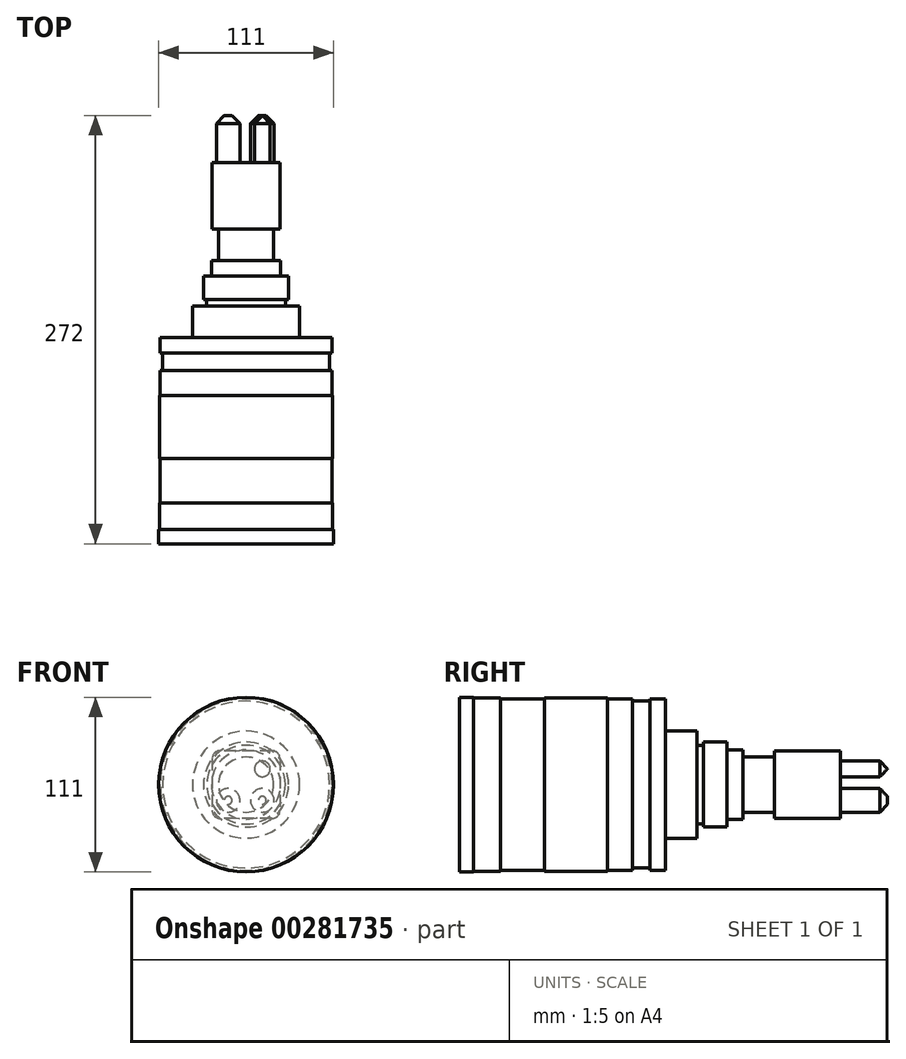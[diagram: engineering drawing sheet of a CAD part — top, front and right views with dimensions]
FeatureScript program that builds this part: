
annotation { "Feature Type Name" : "Feature", "Feature Type Description" : "" }
export const myFeature = defineFeature(function(context is Context, id is Id, definition is map)
    precondition{}
    {
        {
            var Q0;
            Q0=qCreatedBy(makeId("Right.planeOp"),FACE);
            var sketch = newSketch(context, id + "F0", { "sketchPlane" : qUnion([Q0])});
            skLineSegment(sketch, "E0", {"start": v(-113.88, 0) * mm, "end": v(-113.88, 55.5) * mm});
            skLineSegment(sketch, "E1", {"start": v(-113.88, 55.5) * mm, "end": v(-104.88, 55.5) * mm});
            skLineSegment(sketch, "E2", {"start": v(-104.88, 55.5) * mm, "end": v(-104.88, 55) * mm});
            skLineSegment(sketch, "E3", {"start": v(-104.88, 55) * mm, "end": v(-87.88, 55) * mm});
            skLineSegment(sketch, "E4", {"start": v(-87.88, 55) * mm, "end": v(-87.88, 54.5) * mm});
            skLineSegment(sketch, "E5", {"start": v(-87.88, 54.5) * mm, "end": v(-59.88, 54.5) * mm});
            skLineSegment(sketch, "E6", {"start": v(-59.88, 54.5) * mm, "end": v(-59.88, 55) * mm});
            skLineSegment(sketch, "E7", {"start": v(-59.88, 55) * mm, "end": v(-19.88, 55) * mm});
            skLineSegment(sketch, "E8", {"start": v(-19.88, 55) * mm, "end": v(-19.88, 54.5) * mm});
            skLineSegment(sketch, "E9", {"start": v(-19.88, 54.5) * mm, "end": v(-3.88, 54.5) * mm});
            skLineSegment(sketch, "E10", {"start": v(-3.88, 54.5) * mm, "end": v(-3.88, 53) * mm});
            skLineSegment(sketch, "E11", {"start": v(-3.88, 53) * mm, "end": v(7.12, 53) * mm});
            skLineSegment(sketch, "E12", {"start": v(7.12, 53) * mm, "end": v(7.12, 54.5) * mm});
            skLineSegment(sketch, "E13", {"start": v(7.12, 54.5) * mm, "end": v(17.12, 54.5) * mm});
            skLineSegment(sketch, "E14", {"start": v(17.12, 54.5) * mm, "end": v(17.12, 34) * mm});
            skLineSegment(sketch, "E15", {"start": v(17.12, 34) * mm, "end": v(37.12, 34) * mm});
            skLineSegment(sketch, "E16", {"start": v(37.12, 34) * mm, "end": v(37.12, 25) * mm});
            skLineSegment(sketch, "E17", {"start": v(37.12, 25) * mm, "end": v(41.12, 25) * mm});
            skLineSegment(sketch, "E18", {"start": v(41.12, 25) * mm, "end": v(41.12, 27) * mm});
            skLineSegment(sketch, "E19", {"start": v(41.12, 27) * mm, "end": v(56.12, 27) * mm});
            skLineSegment(sketch, "E20", {"start": v(56.12, 27) * mm, "end": v(56.12, 22) * mm});
            skLineSegment(sketch, "E21", {"start": v(56.12, 22) * mm, "end": v(66.12, 22) * mm});
            skLineSegment(sketch, "E22", {"start": v(66.12, 22) * mm, "end": v(66.12, 17.5) * mm});
            skLineSegment(sketch, "E23", {"start": v(66.12, 17.5) * mm, "end": v(86.12, 17.5) * mm});
            skLineSegment(sketch, "E24", {"start": v(86.12, 17.5) * mm, "end": v(86.12, 0) * mm});
            skLineSegment(sketch, "E25", {"start": v(-113.88, 0) * mm, "end": v(86.12, 0) * mm});
            skLineSegment(sketch, "E26", {"start": v(-143.44, 0) * mm, "end": v(122.9, 0) * mm, "construction": true});
            skSolve(sketch);
        }
        {
            var Q0;
            Q0=makeQuery(id+"F0.imprint","IMPRINT",FACE,{"disambiguationData":[TD([[makeQuery(id+"F0.imprint","IMPRINT",EDGE,{"derivedFrom":sQuery(id+"F0.wireOp",EDGE,"E0")}),-1.0]])]});
            var Q1;
            Q1=sQuery(id+"F0.wireOp",EDGE,"E26");
            revolve(context, id + "F1", {"entities" : qUnion([Q0]), "axis" : qUnion([Q1]), "revolveType" : RevolveType.FULL});
        }
        {
            var Q0;
            Q0=makeQuery(id+"F1.opRevolve","SWEPT_FACE",FACE,{"disambiguationData":[OSD([sQuery(id+"F0.wireOp",EDGE,"E24")])]});
            var sketch = newSketch(context, id + "F2", { "sketchPlane" : qUnion([Q0])});
            skLineSegment(sketch, "E27.bottom", {"start": v(-16.5, 21.5) * mm, "end": v(16.5, 21.5) * mm});
            skLineSegment(sketch, "E27.top", {"start": v(-16.5, -21.5) * mm, "end": v(16.5, -21.5) * mm});
            skLineSegment(sketch, "E27.left", {"start": v(-21.5, 16.5) * mm, "end": v(-21.5, -16.5) * mm});
            skLineSegment(sketch, "E27.right", {"start": v(21.5, 16.5) * mm, "end": v(21.5, -16.5) * mm});
            skPoint(sketch, "E27.middle", {"position": v(0, 0) * mm});
            skPoint(sketch, "E28.visualSharp", {"position": v(-21.5, 21.5) * mm});
            skArc(sketch, "E28.filletArc", {"start": v(-16.5, 21.5) * mm, "mid": v(-20.04, 20.04) * mm, "end": v(-21.5, 16.5) * mm});
            skPoint(sketch, "E29.visualSharp", {"position": v(21.5, 21.5) * mm});
            skArc(sketch, "E29.filletArc", {"start": v(21.5, 16.5) * mm, "mid": v(20.04, 20.04) * mm, "end": v(16.5, 21.5) * mm});
            skPoint(sketch, "E30.visualSharp", {"position": v(21.5, -21.5) * mm});
            skArc(sketch, "E30.filletArc", {"start": v(16.5, -21.5) * mm, "mid": v(20.04, -20.04) * mm, "end": v(21.5, -16.5) * mm});
            skPoint(sketch, "E31.visualSharp", {"position": v(-21.5, -21.5) * mm});
            skArc(sketch, "E31.filletArc", {"start": v(-21.5, -16.5) * mm, "mid": v(-20.04, -20.04) * mm, "end": v(-16.5, -21.5) * mm});
            skSolve(sketch);
        }
        {
            var Q0;
            Q0=makeQuery(id+"F2.imprint","IMPRINT",FACE,{"disambiguationData":[TD([[makeQuery(id+"F2.imprint","IMPRINT",EDGE,{"derivedFrom":makeQuery(id+"F1.opRevolve","SWEPT_EDGE",EDGE,{"disambiguationData":[OSD([sQuery(id+"F0.wireOp",EDGE,"E23"),sQuery(id+"F0.wireOp",EDGE,"E24")])]})}),-1.0]])]});
            var Q1;
            Q1=makeQuery(id+"F2.imprint","IMPRINT",FACE,{"disambiguationData":[TD([[makeQuery(id+"F2.imprint","IMPRINT",EDGE,{"derivedFrom":sQuery(id+"F2.wireOp",EDGE,"E27.bottom")}),-1.0]])]});
            extrude(context, id + "F3", {"entities" : qUnion([Q0, Q1]), "depth" : 42 * mm});
        }
        {
            var Q0;
            Q0=makeQuery(id+"F3.opExtrude","CAP_FACE",FACE,{"disambiguationData":[OSD([sQuery(id+"F2.wireOp",EDGE,"E27.bottom"),sQuery(id+"F2.wireOp",EDGE,"E27.top"),sQuery(id+"F2.wireOp",EDGE,"E27.left"),sQuery(id+"F2.wireOp",EDGE,"E27.right"),sQuery(id+"F2.wireOp",EDGE,"E28.filletArc"),sQuery(id+"F2.wireOp",EDGE,"E29.filletArc"),sQuery(id+"F2.wireOp",EDGE,"E30.filletArc"),sQuery(id+"F2.wireOp",EDGE,"E31.filletArc")])],"isStart":false});
            var sketch = newSketch(context, id + "F4", { "sketchPlane" : qUnion([Q0])});
            skCircle(sketch, "E32", {"center": v(-10.33, 9.97) * mm, "radius": 5 * mm});
            skCircle(sketch, "E33", {"center": v(-10.33, -10.03) * mm, "radius": 7.5 * mm});
            skCircle(sketch, "E34", {"center": v(11.38, -10.03) * mm, "radius": 7.5 * mm});
            skLineSegment(sketch, "E35", {"start": v(-10.33, -10.03) * mm, "end": v(11.38, -10.03) * mm, "construction": true});
            skLineSegment(sketch, "E36", {"start": v(-10.33, 9.97) * mm, "end": v(-10.33, -10.03) * mm, "construction": true});
            skSolve(sketch);
        }
        {
            var Q0;
            Q0=makeQuery(id+"F4.imprint","IMPRINT",FACE,{"disambiguationData":[TD([[makeQuery(id+"F4.imprint","IMPRINT",EDGE,{"derivedFrom":sQuery(id+"F4.wireOp",EDGE,"E32")}),1.0]])]});
            var Q1;
            Q1=makeQuery(id+"F4.imprint","IMPRINT",FACE,{"disambiguationData":[TD([[makeQuery(id+"F4.imprint","IMPRINT",EDGE,{"derivedFrom":sQuery(id+"F4.wireOp",EDGE,"E33")}),1.0]])]});
            var Q2;
            Q2=makeQuery(id+"F4.imprint","IMPRINT",FACE,{"disambiguationData":[TD([[makeQuery(id+"F4.imprint","IMPRINT",EDGE,{"derivedFrom":sQuery(id+"F4.wireOp",EDGE,"E34")}),1.0]])]});
            extrude(context, id + "F5", {"entities" : qUnion([Q0, Q1, Q2]), "operationType" : NewBodyOperationType.ADD, "depth" : 30 * mm});
        }
        {
            var Q0;
            Q0=makeQuery(id+"F5.opExtrude","CAP_EDGE",EDGE,{"disambiguationData":[OSD([sQuery(id+"F4.wireOp",EDGE,"E34")])],"isStart":false});
            var Q1;
            Q1=makeQuery(id+"F5.opExtrude","CAP_EDGE",EDGE,{"disambiguationData":[OSD([sQuery(id+"F4.wireOp",EDGE,"E33")])],"isStart":false});
            var Q2;
            Q2=makeQuery(id+"F5.opExtrude","CAP_EDGE",EDGE,{"disambiguationData":[OSD([sQuery(id+"F4.wireOp",EDGE,"E32")])],"isStart":false});
            chamfer(context, id + "F6", {"entities" : qUnion([Q0, Q1, Q2]), "width" : 5 * mm, "tangentPropagation" : true});
        }
    });
